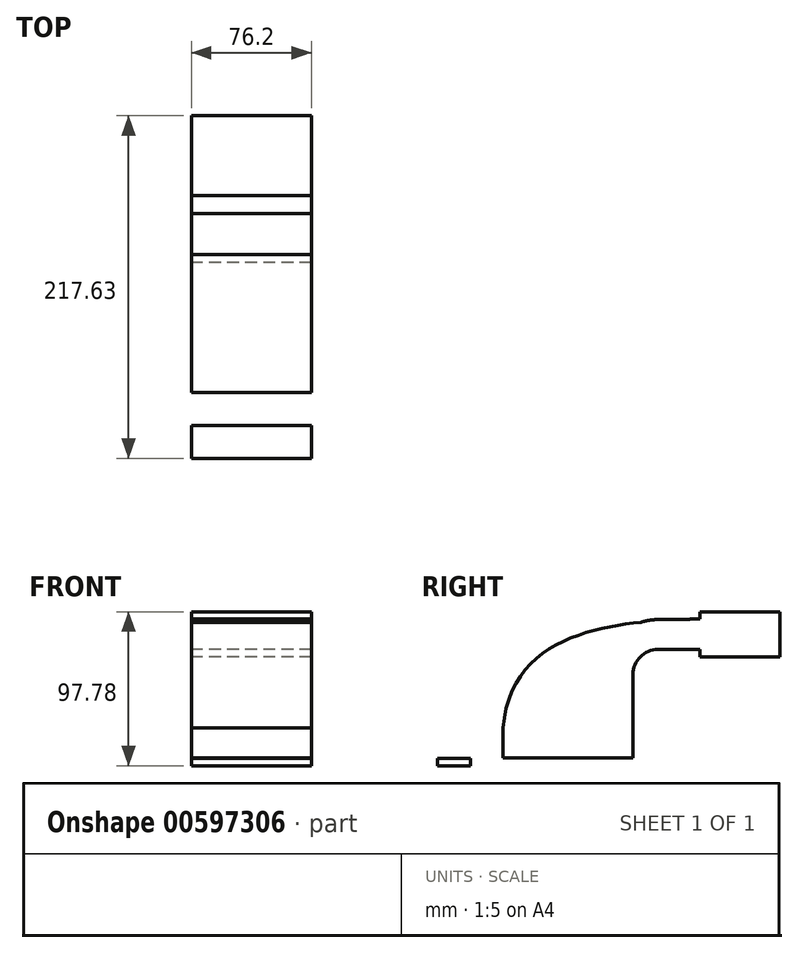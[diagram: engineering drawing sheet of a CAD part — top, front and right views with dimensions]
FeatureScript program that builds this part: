
annotation { "Feature Type Name" : "Feature", "Feature Type Description" : "" }
export const myFeature = defineFeature(function(context is Context, id is Id, definition is map)
    precondition{}
    {
        {
            var Q0;
            Q0=qCreatedBy(makeId("Right.planeOp"),FACE);
            var sketch = newSketch(context, id + "F0", { "sketchPlane" : qUnion([Q0])});
            skLineSegment(sketch, "E0.bottom", {"start": v(-41.28, 9.52) * mm, "end": v(41.28, 9.52) * mm});
            skLineSegment(sketch, "E0.top", {"start": v(-41.28, -9.53) * mm, "end": v(41.28, -9.53) * mm});
            skLineSegment(sketch, "E0.left", {"start": v(-41.28, 9.52) * mm, "end": v(-41.28, -9.53) * mm});
            skLineSegment(sketch, "E0.right", {"start": v(41.28, 9.52) * mm, "end": v(41.28, -9.53) * mm});
            skPoint(sketch, "E0.middle", {"position": v(0, 0) * mm});
            skLineSegment(sketch, "E1.bottom", {"start": v(-62.05, -14.6) * mm, "end": v(-83.02, -14.6) * mm});
            skLineSegment(sketch, "E1.top", {"start": v(-62.05, -9.92) * mm, "end": v(-83.02, -9.92) * mm});
            skLineSegment(sketch, "E1.left", {"start": v(-62.05, -14.6) * mm, "end": v(-62.05, -9.92) * mm});
            skLineSegment(sketch, "E1.right", {"start": v(-83.02, -14.6) * mm, "end": v(-83.02, -9.92) * mm});
            skLineSegment(sketch, "E2.bottom", {"start": v(134.61, 83.18) * mm, "end": v(83.81, 83.18) * mm});
            skLineSegment(sketch, "E2.top", {"start": v(134.61, 54.6) * mm, "end": v(83.81, 54.6) * mm});
            skLineSegment(sketch, "E2.left", {"start": v(134.61, 83.18) * mm, "end": v(134.61, 54.6) * mm});
            skLineSegment(sketch, "E2.right", {"start": v(83.81, 83.18) * mm, "end": v(83.81, 54.6) * mm});
            skPoint(sketch, "E2.middle", {"position": v(109.21, 68.9) * mm});
            skLineSegment(sketch, "E3", {"start": v(41.28, 43.35) * mm, "end": v(41.28, 9.52) * mm});
            skPoint(sketch, "E4.endSnap0", {"position": v(109.21, 54.6) * mm});
            skArc(sketch, "E5", {"start": v(57.15, 59.23) * mm, "mid": v(45.92, 54.58) * mm, "end": v(41.28, 43.35) * mm});
            skLineSegment(sketch, "E6", {"start": v(57.15, 59.23) * mm, "end": v(109.21, 59.23) * mm});
            skLineSegment(sketch, "E7.0", {"start": v(22.22, 43.35) * mm, "end": v(22.22, 9.52) * mm});
            skArc(sketch, "E7.1", {"start": v(57.15, 78.28) * mm, "mid": v(32.45, 68.05) * mm, "end": v(22.23, 43.35) * mm});
            skLineSegment(sketch, "E7.2", {"start": v(57.15, 78.28) * mm, "end": v(110.38, 78.28) * mm});
            skFitSpline(sketch, "E8", {"points": [v(-41.28, 9.53) * mm, v(72.37, 78.28) * mm, v(110.38, 78.28) * mm], "startDerivative": vector(23.08, 296.07) * mm, "endDerivative": vector(86.35, -12.2) * mm});
            skPoint(sketch, "E9.1.internal.snap0", {"position": v(109.21, 83.18) * mm});
            skSolve(sketch);
        }
        {
            var Q0;
            Q0=makeQuery(id+"F0.imprint","IMPRINT",FACE,{"disambiguationData":[TD([[makeQuery(id+"F0.imprint","IMPRINT",EDGE,{"derivedFrom":sQuery(id+"F0.wireOp",EDGE,"E1.bottom")}),-1.0]])]});
            var Q1;
            {var subQ0=sQuery(id+"F0.wireOp",EDGE,"E7.2");var subQ1=sQuery(id+"F0.wireOp",EDGE,"E7.1");var subQ2=makeQuery(id+"F0.imprint","INTERSECT",VERTEX,{"derivedFrom":[subQ1,subQ0]});Q1=makeQuery(id+"F0.imprint","IMPRINT",FACE,{"disambiguationData":[TD([[makeQuery(id+"F0.imprint","IMPRINT",EDGE,{"disambiguationData":[TD([[subQ2,-1.0]])],"derivedFrom":subQ1}),1.0]])]});}
            var Q2;
            Q2=makeQuery(id+"F0.imprint","IMPRINT",FACE,{"disambiguationData":[TD([[makeQuery(id+"F0.imprint","IMPRINT",EDGE,{"derivedFrom":sQuery(id+"F0.wireOp",EDGE,"E0.top")}),1.0]])]});
            var Q3;
            {var subQ1=sQuery(id+"F0.wireOp",EDGE,"E2.bottom");Q3=makeQuery(id+"F0.imprint","IMPRINT",FACE,{"disambiguationData":[TD([[makeQuery(id+"F0.imprint","IMPRINT",EDGE,{"derivedFrom":subQ1}),1.0]])]});}
            var Q4;
            {var subQ0=sQuery(id+"F0.wireOp",EDGE,"E8");var subQ1=sQuery(id+"F0.wireOp",EDGE,"E2.right");var subQ2=makeQuery(id+"F0.imprint","INTERSECT",VERTEX,{"derivedFrom":[subQ1,subQ0]});Q4=makeQuery(id+"F0.imprint","IMPRINT",FACE,{"disambiguationData":[TD([[makeQuery(id+"F0.imprint","IMPRINT",EDGE,{"disambiguationData":[TD([[subQ2,-1.0]])],"derivedFrom":subQ1}),-1.0]])]});}
            var Q5;
            {var subQ0=sQuery(id+"F0.wireOp",EDGE,"E8");var subQ1=sQuery(id+"F0.wireOp",EDGE,"E2.right");var subQ2=makeQuery(id+"F0.imprint","INTERSECT",VERTEX,{"derivedFrom":[subQ1,subQ0]});Q5=makeQuery(id+"F0.imprint","IMPRINT",FACE,{"disambiguationData":[TD([[makeQuery(id+"F0.imprint","IMPRINT",EDGE,{"disambiguationData":[TD([[subQ2,-1.0]])],"derivedFrom":subQ1}),1.0]])]});}
            var Q6;
            {var subQ6=sQuery(id+"F0.wireOp",EDGE,"E3");Q6=makeQuery(id+"F0.imprint","IMPRINT",FACE,{"disambiguationData":[TD([[makeQuery(id+"F0.imprint","IMPRINT",EDGE,{"derivedFrom":subQ6}),-1.0]])]});}
            var Q7;
            {var subQ3=sQuery(id+"F0.wireOp",EDGE,"E7.0");Q7=makeQuery(id+"F0.imprint","IMPRINT",FACE,{"disambiguationData":[TD([[makeQuery(id+"F0.imprint","IMPRINT",EDGE,{"derivedFrom":subQ3}),-1.0]])]});}
            var Q8;
            {var subQ3=sQuery(id+"F0.wireOp",EDGE,"E7.0");Q8=makeQuery(id+"F0.imprint","IMPRINT",FACE,{"disambiguationData":[TD([[makeQuery(id+"F0.imprint","IMPRINT",EDGE,{"derivedFrom":subQ3}),-1.0]])]});}
            extrude(context, id + "F1", {"entities" : qUnion([Q0, Q1, Q2, Q3, Q4, Q5, Q6, Q7, Q8]), "endBound" : BoundingType.SYMMETRIC, "depth" : 76.2 * mm, "offsetDistance" : 25.4 * mm});
        }
    });
